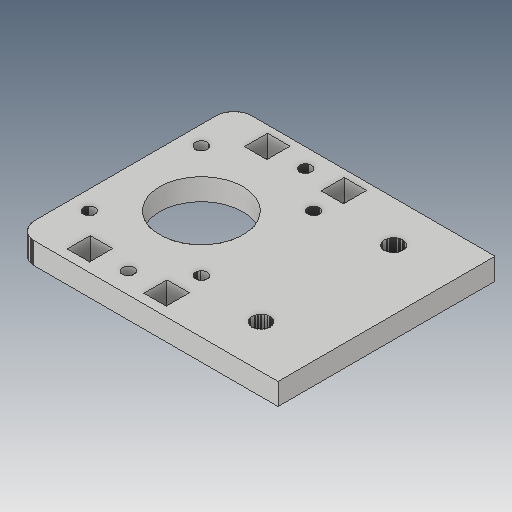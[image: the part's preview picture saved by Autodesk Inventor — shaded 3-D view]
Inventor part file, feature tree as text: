
AUTODESK INVENTOR PART (.ipt)
format: ipt  version: 2017 (Build 210142000, 142)  size: 1,031,168 bytes
history: native  units: mm
features: sketch x4, other x3
ambient origin geometry x8: Origin, YZ Plane, XZ Plane, XY Plane, X Axis, Y Axis, Z Axis, Center Point
bodies: Solid1 (feature_tree)
feature tree (7):
  other  "Y-Motor-Mount Top.ipt"
  other  "Solid1::Y-Motor-Mount Top.ipt"
  other  "TaggingFeature1"
  sketch  "Sketch1"  dims[d0=10.0mm]
  sketch  "Sketch2"
  sketch  "Sketch3"
  sketch  "Sketch4"
